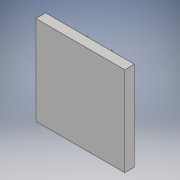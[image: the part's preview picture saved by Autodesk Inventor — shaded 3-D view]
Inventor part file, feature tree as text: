
AUTODESK INVENTOR PART (.ipt)
format: ipt  version: 2018 (Build 220112000, 112)  size: 137,728 bytes
history: native  units: in
note: dims shown in document units (in); Inventor stores cm internally (conversion verified against a paired STEP export)
features: sketch x4, extrude x3
ambient origin geometry x8: Origin, YZ Plane, XZ Plane, XY Plane, X Axis, Y Axis, Z Axis, Center Point
bodies: Body1 (feature_tree)
feature tree (7):
  sketch  "Sketch4"  dims[d9=0.5in d12=1.0in d13=0.0in]
  sketch  "Sketch5"  dims[d14=0.5in d15=0.0in d16=0.5in d17=0.0in]
  extrude  "Extrusion4"  Depth=1.0in TaperAngle=0.0deg
  extrude  "Extrusion5"  Depth=0.5in TaperAngle=0.0deg
  extrude  "Extrusion6"  [1 undecoded]
  sketch  "Sketch7"
  sketch  "Sketch6"
note: 1 required parameter value undecoded (feature->parameter linkage not recoverable at this tier; creation-order binding heuristic only, values carry confidence <= 0.55)
